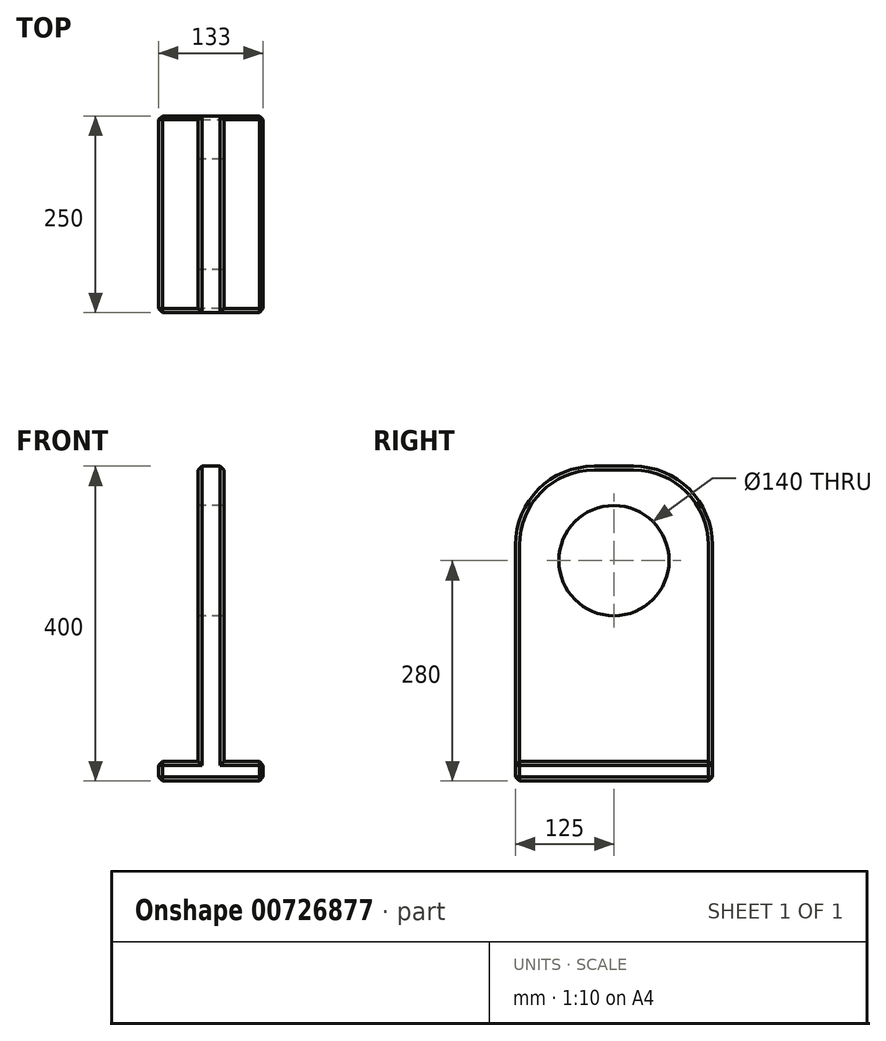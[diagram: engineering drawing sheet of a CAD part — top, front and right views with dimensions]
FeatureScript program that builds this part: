
annotation { "Feature Type Name" : "Feature", "Feature Type Description" : "" }
export const myFeature = defineFeature(function(context is Context, id is Id, definition is map)
    precondition{}
    {
        {
            var Q0;
            Q0=qCreatedBy(makeId("Front.planeOp"),FACE);
            var sketch = newSketch(context, id + "F0", { "sketchPlane" : qUnion([Q0])});
            skLineSegment(sketch, "E0", {"start": v(0, 0) * mm, "end": v(0, 400) * mm});
            skLineSegment(sketch, "E1", {"start": v(0, 400) * mm, "end": v(33, 400) * mm});
            skLineSegment(sketch, "E2", {"start": v(33, 400) * mm, "end": v(33, 0) * mm});
            skLineSegment(sketch, "E3", {"start": v(33, 0) * mm, "end": v(0, 0) * mm});
            skLineSegment(sketch, "E4", {"start": v(33, 0) * mm, "end": v(83, 0) * mm});
            skLineSegment(sketch, "E5", {"start": v(83, 0) * mm, "end": v(83, 25) * mm});
            skLineSegment(sketch, "E6", {"start": v(83, 25) * mm, "end": v(33, 25) * mm});
            skLineSegment(sketch, "E7", {"start": v(33, 25) * mm, "end": v(33, 0) * mm});
            skLineSegment(sketch, "E8", {"start": v(0, 0) * mm, "end": v(-50, 0) * mm});
            skLineSegment(sketch, "E9", {"start": v(-50, 0) * mm, "end": v(-50, 25) * mm});
            skLineSegment(sketch, "E10", {"start": v(-50, 25) * mm, "end": v(0, 25) * mm});
            skSolve(sketch);
        }
        {
            var Q0;
            {var subQ0=sQuery(id+"F0.wireOp",EDGE,"E1");Q0=makeQuery(id+"F0.imprint","IMPRINT",FACE,{"disambiguationData":[TD([[makeQuery(id+"F0.imprint","IMPRINT",EDGE,{"derivedFrom":subQ0}),-1.0]])]});}
            var Q1;
            {var subQ0=sQuery(id+"F0.wireOp",EDGE,"E8");Q1=makeQuery(id+"F0.imprint","IMPRINT",FACE,{"disambiguationData":[TD([[makeQuery(id+"F0.imprint","IMPRINT",EDGE,{"derivedFrom":subQ0}),-1.0]])]});}
            var Q2;
            Q2=makeQuery(id+"F0.imprint","IMPRINT",FACE,{"disambiguationData":[TD([[makeQuery(id+"F0.imprint","IMPRINT",EDGE,{"derivedFrom":sQuery(id+"F0.wireOp",EDGE,"E4")}),1.0]])]});
            extrude(context, id + "F1", {"entities" : qUnion([Q0, Q1, Q2]), "depth" : 250 * mm, "offsetDistance" : 25 * mm});
        }
        {
            var Q0;
            Q0=makeQuery(id+"F1.opExtrude","SWEPT_FACE",FACE,{"disambiguationData":[OSD([sQuery(id+"F0.wireOp",EDGE,"E2")])]});
            var sketch = newSketch(context, id + "F2", { "sketchPlane" : qUnion([Q0])});
            skLineSegment(sketch, "E11", {"start": v(-250, 400) * mm, "end": v(-125, 400) * mm});
            skLineSegment(sketch, "E12", {"start": v(-125, 400) * mm, "end": v(-125, 280) * mm});
            skPoint(sketch, "E13", {"position": v(-125, 280) * mm});
            skSolve(sketch);
        }
        {
            var Q0;
            Q0=sQuery(id+"F2.wireOp",VERTEX,"E13");
            var Q1;
            Q1=makeQuery(id+"F1.opExtrude","SWEPT_BODY",BODY,{"disambiguationData":[OSD([sQuery(id+"F0.wireOp",EDGE,"E0"),sQuery(id+"F0.wireOp",EDGE,"E1"),sQuery(id+"F0.wireOp",EDGE,"E2"),sQuery(id+"F0.wireOp",EDGE,"E3"),sQuery(id+"F0.wireOp",EDGE,"E4"),sQuery(id+"F0.wireOp",EDGE,"E5"),sQuery(id+"F0.wireOp",EDGE,"E6"),sQuery(id+"F0.wireOp",EDGE,"E8"),sQuery(id+"F0.wireOp",EDGE,"E9"),sQuery(id+"F0.wireOp",EDGE,"E10")])]});
            hole(context, id + "F3", {"style" : HoleStyle.SIMPLE, "endStyle" : HoleEndStyle.BLIND, "holeDiameter" : 140 * mm, "majorDiameter" : 5 * mm, "holeDepth" : 60 * mm, "isTappedThrough" : true, "tappedDepth" : 12 * mm, "tapClearance" : 3, "locations" : qUnion([Q0]), "scope" : qUnion([Q1])});
        }
        {
            var Q0;
            Q0=makeQuery(id+"F1.opExtrude","CAP_EDGE",EDGE,{"disambiguationData":[OSD([sQuery(id+"F0.wireOp",EDGE,"E1")])],"isStart":true});
            var Q1;
            Q1=makeQuery(id+"F1.opExtrude","CAP_EDGE",EDGE,{"disambiguationData":[OSD([sQuery(id+"F0.wireOp",EDGE,"E1")])],"isStart":false});
            fillet(context, id + "F4", {"entities" : qUnion([Q0, Q1]), "radius" : 100 * mm, "tangentPropagation" : true, "allowEdgeOverflow" : false});
        }
        {
            var Q0;
            Q0=makeQuery(id+"F1.opExtrude","SWEPT_EDGE",EDGE,{"disambiguationData":[OSD([sQuery(id+"F0.wireOp",EDGE,"E9"),sQuery(id+"F0.wireOp",EDGE,"E10")])]});
            var Q1;
            Q1=makeQuery(id+"F1.opExtrude","SWEPT_EDGE",EDGE,{"disambiguationData":[OSD([sQuery(id+"F0.wireOp",EDGE,"E8"),sQuery(id+"F0.wireOp",EDGE,"E9")])]});
            var Q2;
            Q2=makeQuery(id+"F1.opExtrude","CAP_EDGE",EDGE,{"disambiguationData":[OSD([sQuery(id+"F0.wireOp",EDGE,"E9")])],"isStart":true});
            var Q3;
            Q3=makeQuery(id+"F1.opExtrude","CAP_EDGE",EDGE,{"disambiguationData":[OSD([sQuery(id+"F0.wireOp",EDGE,"E9")])],"isStart":false});
            var Q4;
            Q4=makeQuery(id+"F1.opExtrude","CAP_EDGE",EDGE,{"disambiguationData":[OSD([sQuery(id+"F0.wireOp",EDGE,"E10")])],"isStart":false});
            var Q5;
            Q5=makeQuery(id+"F1.opExtrude","CAP_EDGE",EDGE,{"disambiguationData":[OSD([sQuery(id+"F0.wireOp",EDGE,"E0")])],"isStart":false});
            var Q6;
            Q6=makeQuery(id+"F1.opExtrude","CAP_EDGE",EDGE,{"disambiguationData":[OSD([sQuery(id+"F0.wireOp",EDGE,"E2")])],"isStart":false});
            var Q7;
            Q7=makeQuery(id+"F1.opExtrude","CAP_EDGE",EDGE,{"disambiguationData":[OSD([sQuery(id+"F0.wireOp",EDGE,"E10")])],"isStart":true});
            var Q8;
            Q8=makeQuery(id+"F1.opExtrude","CAP_EDGE",EDGE,{"disambiguationData":[OSD([sQuery(id+"F0.wireOp",EDGE,"E3"),sQuery(id+"F0.wireOp",EDGE,"E4"),sQuery(id+"F0.wireOp",EDGE,"E8")])],"isStart":true});
            var Q9;
            Q9=makeQuery(id+"F1.opExtrude","CAP_EDGE",EDGE,{"disambiguationData":[OSD([sQuery(id+"F0.wireOp",EDGE,"E6")])],"isStart":true});
            var Q10;
            Q10=makeQuery(id+"F1.opExtrude","CAP_EDGE",EDGE,{"disambiguationData":[OSD([sQuery(id+"F0.wireOp",EDGE,"E5")])],"isStart":true});
            var Q11;
            Q11=makeQuery(id+"F1.opExtrude","SWEPT_EDGE",EDGE,{"disambiguationData":[OSD([sQuery(id+"F0.wireOp",EDGE,"E5"),sQuery(id+"F0.wireOp",EDGE,"E6")])]});
            var Q12;
            Q12=makeQuery(id+"F1.opExtrude","SWEPT_EDGE",EDGE,{"disambiguationData":[OSD([sQuery(id+"F0.wireOp",EDGE,"E4"),sQuery(id+"F0.wireOp",EDGE,"E5")])]});
            var Q13;
            Q13=makeQuery(id+"F1.opExtrude","CAP_EDGE",EDGE,{"disambiguationData":[OSD([sQuery(id+"F0.wireOp",EDGE,"E5")])],"isStart":false});
            var Q14;
            Q14=makeQuery(id+"F1.opExtrude","CAP_EDGE",EDGE,{"disambiguationData":[OSD([sQuery(id+"F0.wireOp",EDGE,"E6")])],"isStart":false});
            var Q15;
            Q15=makeQuery(id+"F1.opExtrude","CAP_EDGE",EDGE,{"disambiguationData":[OSD([sQuery(id+"F0.wireOp",EDGE,"E3"),sQuery(id+"F0.wireOp",EDGE,"E4"),sQuery(id+"F0.wireOp",EDGE,"E8")])],"isStart":false});
            chamfer(context, id + "F5", {"entities" : qUnion([Q0, Q1, Q2, Q3, Q4, Q5, Q6, Q7, Q8, Q9, Q10, Q11, Q12, Q13, Q14, Q15]), "width" : 5 * mm, "tangentPropagation" : true});
        }
    });
